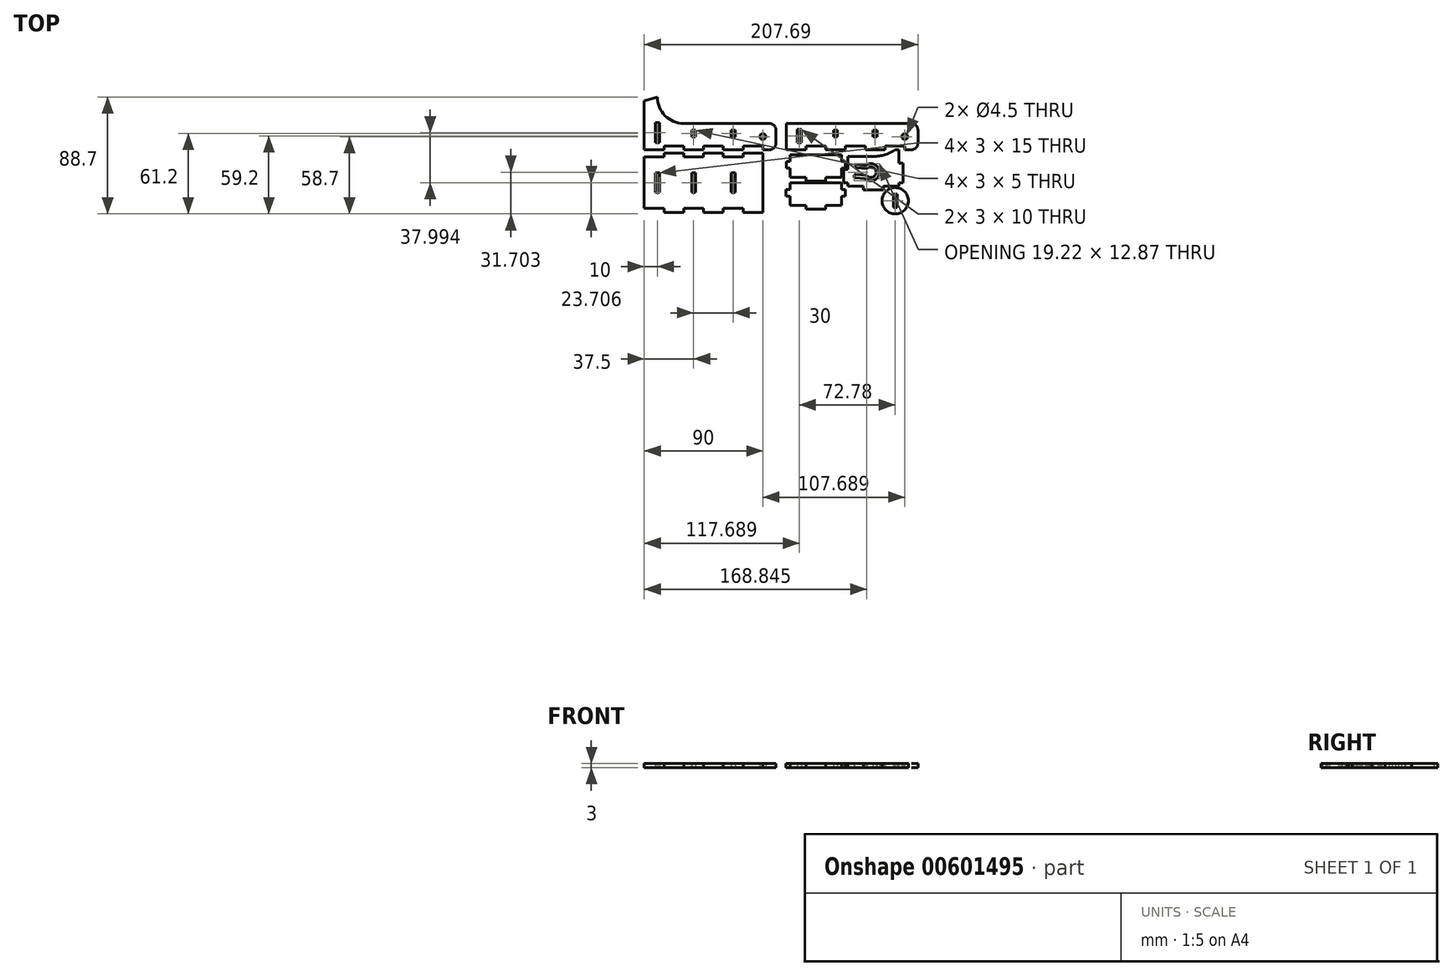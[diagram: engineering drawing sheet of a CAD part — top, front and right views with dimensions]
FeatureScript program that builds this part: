
annotation { "Feature Type Name" : "Feature", "Feature Type Description" : "" }
export const myFeature = defineFeature(function(context is Context, id is Id, definition is map)
    precondition{}
    {
        {
            assignVariable(context, id + "F0", {"name" : "woodTh", "anyValue" : 3});
        }
        {
            var Q0;
            Q0=qCreatedBy(makeId("Top.planeOp"),FACE);
            var sketch = newSketch(context, id + "F1", { "sketchPlane" : qUnion([Q0])});
            skLineSegment(sketch, "E0", {"start": v(10, 40) * mm, "end": v(10, 40) * mm});
            skLineSegment(sketch, "E1", {"start": v(100, 10) * mm, "end": v(90, 10) * mm, "construction": true});
            skCircle(sketch, "E2", {"center": v(90, 10) * mm, "radius": 2.25 * mm});
            skPoint(sketch, "E3.visualSharp", {"position": v(10, 17.5) * mm});
            skArc(sketch, "E3.filletArc", {"start": v(10, 40) * mm, "mid": v(15.86, 25.86) * mm, "end": v(30, 20) * mm});
            skLineSegment(sketch, "E4", {"start": v(0, 0) * mm, "end": v(15, 0) * mm});
            skLineSegment(sketch, "E5", {"start": v(15, 0) * mm, "end": v(15, 3) * mm});
            skLineSegment(sketch, "E6", {"start": v(15, 3) * mm, "end": v(30, 3) * mm});
            skLineSegment(sketch, "E7", {"start": v(30, 3) * mm, "end": v(30, 0) * mm});
            skLineSegment(sketch, "E8.1.0.0", {"start": v(30, 0) * mm, "end": v(45, 0) * mm});
            skLineSegment(sketch, "E8.1.0.1", {"start": v(60, 3) * mm, "end": v(60, 0) * mm});
            skLineSegment(sketch, "E8.1.0.2", {"start": v(45, 3) * mm, "end": v(60, 3) * mm});
            skLineSegment(sketch, "E8.1.0.3", {"start": v(45, 0) * mm, "end": v(45, 3) * mm});
            skLineSegment(sketch, "E8.2.0.0", {"start": v(60, 0) * mm, "end": v(75, 0) * mm});
            skLineSegment(sketch, "E8.2.0.1", {"start": v(90, 3) * mm, "end": v(90, 0) * mm});
            skLineSegment(sketch, "E8.2.0.2", {"start": v(75, 3) * mm, "end": v(90, 3) * mm});
            skLineSegment(sketch, "E8.2.0.3", {"start": v(75, 0) * mm, "end": v(75, 3) * mm});
            skLineSegment(sketch, "E8.direction1", {"start": v(0, 0) * mm, "end": v(30, 0) * mm, "construction": true});
            skLineSegment(sketch, "E9", {"start": v(30, 20) * mm, "end": v(95, 20) * mm});
            skLineSegment(sketch, "E10", {"start": v(100, 15) * mm, "end": v(100, 5) * mm});
            skLineSegment(sketch, "E11", {"start": v(95, 0) * mm, "end": v(90, 0) * mm});
            skPoint(sketch, "E12.visualSharp", {"position": v(100, 20) * mm});
            skArc(sketch, "E12.filletArc", {"start": v(100, 15) * mm, "mid": v(98.54, 18.54) * mm, "end": v(95, 20) * mm});
            skPoint(sketch, "E13.visualSharp", {"position": v(100, 0) * mm});
            skArc(sketch, "E13.filletArc", {"start": v(95, 0) * mm, "mid": v(98.54, 1.46) * mm, "end": v(100, 5) * mm});
            skLineSegment(sketch, "E14", {"start": v(37.5, 20) * mm, "end": v(37.5, 12.5) * mm, "construction": true});
            skPoint(sketch, "E14.startSnap0", {"position": v(37.5, 0) * mm});
            skLineSegment(sketch, "E15.bottom", {"start": v(39, 10) * mm, "end": v(36, 10) * mm});
            skLineSegment(sketch, "E15.top", {"start": v(39, 15) * mm, "end": v(36, 15) * mm});
            skLineSegment(sketch, "E15.left", {"start": v(39, 10) * mm, "end": v(39, 15) * mm});
            skLineSegment(sketch, "E15.right", {"start": v(36, 10) * mm, "end": v(36, 15) * mm});
            skPoint(sketch, "E15.middle", {"position": v(37.5, 12.5) * mm});
            skLineSegment(sketch, "E16", {"start": v(52.5, 3) * mm, "end": v(52.5, 20) * mm, "construction": true});
            skLineSegment(sketch, "E17.MirrorCS", {"start": v(66, 10) * mm, "end": v(66, 15) * mm});
            skPoint(sketch, "E18.MirrorP", {"position": v(67.5, 12.5) * mm});
            skLineSegment(sketch, "E19.MirrorCS", {"start": v(69, 10) * mm, "end": v(69, 15) * mm});
            skLineSegment(sketch, "E20.MirrorCS", {"start": v(66, 10) * mm, "end": v(69, 10) * mm});
            skLineSegment(sketch, "E21.MirrorCS", {"start": v(66, 15) * mm, "end": v(69, 15) * mm});
            skLineSegment(sketch, "E22.MirrorCS", {"start": v(67.5, 20) * mm, "end": v(67.5, 12.5) * mm, "construction": true});
            skLineSegment(sketch, "E23", {"start": v(207.69, 10) * mm, "end": v(197.69, 10) * mm, "construction": true});
            skCircle(sketch, "E24", {"center": v(197.69, 10) * mm, "radius": 2.25 * mm});
            skLineSegment(sketch, "E25", {"start": v(107.69, 0) * mm, "end": v(122.69, 0) * mm});
            skLineSegment(sketch, "E26", {"start": v(122.69, 0) * mm, "end": v(122.69, 3) * mm});
            skLineSegment(sketch, "E27", {"start": v(122.69, 3) * mm, "end": v(137.69, 3) * mm});
            skLineSegment(sketch, "E28", {"start": v(137.69, 3) * mm, "end": v(137.69, 0) * mm});
            skLineSegment(sketch, "E29.1.0.0", {"start": v(137.69, 0) * mm, "end": v(152.69, 0) * mm});
            skLineSegment(sketch, "E29.1.0.1", {"start": v(167.69, 3) * mm, "end": v(167.69, 0) * mm});
            skLineSegment(sketch, "E29.1.0.2", {"start": v(152.69, 3) * mm, "end": v(167.69, 3) * mm});
            skLineSegment(sketch, "E29.1.0.3", {"start": v(152.69, 0) * mm, "end": v(152.69, 3) * mm});
            skLineSegment(sketch, "E29.2.0.0", {"start": v(167.69, 0) * mm, "end": v(182.69, 0) * mm});
            skLineSegment(sketch, "E29.2.0.1", {"start": v(197.69, 3) * mm, "end": v(197.69, 0) * mm});
            skLineSegment(sketch, "E29.2.0.2", {"start": v(182.69, 3) * mm, "end": v(197.69, 3) * mm});
            skLineSegment(sketch, "E29.2.0.3", {"start": v(182.69, 0) * mm, "end": v(182.69, 3) * mm});
            skLineSegment(sketch, "E29.direction1", {"start": v(107.69, 0) * mm, "end": v(137.69, 0) * mm, "construction": true});
            skLineSegment(sketch, "E30", {"start": v(137.69, 20) * mm, "end": v(202.69, 20) * mm});
            skLineSegment(sketch, "E31", {"start": v(207.69, 15) * mm, "end": v(207.69, 5) * mm});
            skLineSegment(sketch, "E32", {"start": v(202.69, 0) * mm, "end": v(197.69, 0) * mm});
            skPoint(sketch, "E33.visualSharp", {"position": v(207.69, 20) * mm});
            skArc(sketch, "E33.filletArc", {"start": v(207.69, 15) * mm, "mid": v(206.22, 18.54) * mm, "end": v(202.69, 20) * mm});
            skPoint(sketch, "E34.visualSharp", {"position": v(207.69, 0) * mm});
            skArc(sketch, "E34.filletArc", {"start": v(202.69, 0) * mm, "mid": v(206.22, 1.46) * mm, "end": v(207.69, 5) * mm});
            skLineSegment(sketch, "E35", {"start": v(145.19, 20) * mm, "end": v(145.19, 12.5) * mm, "construction": true});
            skPoint(sketch, "E35.startSnap0", {"position": v(145.19, 0) * mm});
            skLineSegment(sketch, "E36.bottom", {"start": v(146.69, 10) * mm, "end": v(143.69, 10) * mm});
            skLineSegment(sketch, "E36.top", {"start": v(146.69, 15) * mm, "end": v(143.69, 15) * mm});
            skLineSegment(sketch, "E36.left", {"start": v(146.69, 10) * mm, "end": v(146.69, 15) * mm});
            skLineSegment(sketch, "E36.right", {"start": v(143.69, 10) * mm, "end": v(143.69, 15) * mm});
            skPoint(sketch, "E36.middle", {"position": v(145.19, 12.5) * mm});
            skLineSegment(sketch, "E37", {"start": v(160.19, 3) * mm, "end": v(160.19, 20) * mm, "construction": true});
            skLineSegment(sketch, "E38.MirrorCS", {"start": v(173.69, 10) * mm, "end": v(173.69, 15) * mm});
            skPoint(sketch, "E39.MirrorP", {"position": v(175.19, 12.5) * mm});
            skLineSegment(sketch, "E40.MirrorCS", {"start": v(176.69, 10) * mm, "end": v(176.69, 15) * mm});
            skLineSegment(sketch, "E41.MirrorCS", {"start": v(173.69, 10) * mm, "end": v(176.69, 10) * mm});
            skLineSegment(sketch, "E42.MirrorCS", {"start": v(173.69, 15) * mm, "end": v(176.69, 15) * mm});
            skLineSegment(sketch, "E43.MirrorCS", {"start": v(175.19, 20) * mm, "end": v(175.19, 12.5) * mm, "construction": true});
            skCircle(sketch, "E44", {"center": v(190.47, -38.7) * mm, "radius": 10 * mm});
            skLineSegment(sketch, "E45.bottom", {"start": v(191.97, -43.7) * mm, "end": v(188.97, -43.7) * mm});
            skLineSegment(sketch, "E45.top", {"start": v(191.97, -33.7) * mm, "end": v(188.97, -33.7) * mm});
            skLineSegment(sketch, "E45.left", {"start": v(191.97, -43.7) * mm, "end": v(191.97, -33.7) * mm});
            skLineSegment(sketch, "E45.right", {"start": v(188.97, -43.7) * mm, "end": v(188.97, -33.7) * mm});
            skLineSegment(sketch, "E46", {"start": v(0, -5.5) * mm, "end": v(15, -5.5) * mm});
            skLineSegment(sketch, "E47", {"start": v(15, -5.5) * mm, "end": v(15, -2.5) * mm});
            skLineSegment(sketch, "E48", {"start": v(15, -2.5) * mm, "end": v(30, -2.5) * mm});
            skLineSegment(sketch, "E49", {"start": v(30, -2.5) * mm, "end": v(30, -5.5) * mm});
            skLineSegment(sketch, "E50.1.0.0", {"start": v(30, -5.5) * mm, "end": v(45, -5.5) * mm});
            skLineSegment(sketch, "E50.1.0.1", {"start": v(60, -2.5) * mm, "end": v(60, -5.5) * mm});
            skLineSegment(sketch, "E50.1.0.2", {"start": v(45, -2.5) * mm, "end": v(60, -2.5) * mm});
            skLineSegment(sketch, "E50.1.0.3", {"start": v(45, -5.5) * mm, "end": v(45, -2.5) * mm});
            skLineSegment(sketch, "E50.2.0.0", {"start": v(60, -5.5) * mm, "end": v(75, -5.5) * mm});
            skLineSegment(sketch, "E50.2.0.1", {"start": v(90, -2.5) * mm, "end": v(90, -5.5) * mm});
            skLineSegment(sketch, "E50.2.0.2", {"start": v(75, -2.5) * mm, "end": v(90, -2.5) * mm});
            skLineSegment(sketch, "E50.2.0.3", {"start": v(75, -5.5) * mm, "end": v(75, -2.5) * mm});
            skLineSegment(sketch, "E50.direction1", {"start": v(0, -5.5) * mm, "end": v(30, -5.5) * mm, "construction": true});
            skPoint(sketch, "E51.startSnap0", {"position": v(37.5, -5.5) * mm});
            skLineSegment(sketch, "E52", {"start": v(0, -5.5) * mm, "end": v(0, -25) * mm});
            skLineSegment(sketch, "E53", {"start": v(90, -5.5) * mm, "end": v(90, -25) * mm});
            skLineSegment(sketch, "E54", {"start": v(0, -25) * mm, "end": v(90, -25) * mm, "construction": true});
            skLineSegment(sketch, "E55.MirrorCS", {"start": v(45, -44.5) * mm, "end": v(45, -47.5) * mm});
            skLineSegment(sketch, "E56.MirrorCS", {"start": v(75, -44.5) * mm, "end": v(75, -47.5) * mm});
            skLineSegment(sketch, "E57.MirrorCS", {"start": v(30, -47.5) * mm, "end": v(30, -44.5) * mm});
            skLineSegment(sketch, "E58.MirrorCS", {"start": v(90, -47.5) * mm, "end": v(90, -44.5) * mm});
            skLineSegment(sketch, "E59.MirrorCS", {"start": v(60, -47.5) * mm, "end": v(60, -44.5) * mm});
            skLineSegment(sketch, "E60.MirrorCS", {"start": v(15, -44.5) * mm, "end": v(15, -47.5) * mm});
            skLineSegment(sketch, "E61.MirrorCS", {"start": v(0, -44.5) * mm, "end": v(15, -44.5) * mm});
            skLineSegment(sketch, "E62.MirrorCS", {"start": v(0, -44.5) * mm, "end": v(0, -25) * mm});
            skLineSegment(sketch, "E63.MirrorCS", {"start": v(45, -47.5) * mm, "end": v(60, -47.5) * mm});
            skLineSegment(sketch, "E64.MirrorCS", {"start": v(90, -44.5) * mm, "end": v(90, -25) * mm});
            skPoint(sketch, "E65.MirrorP", {"position": v(37.5, -44.5) * mm});
            skLineSegment(sketch, "E66.MirrorCS", {"start": v(30, -44.5) * mm, "end": v(45, -44.5) * mm});
            skLineSegment(sketch, "E67.MirrorCS", {"start": v(75, -47.5) * mm, "end": v(90, -47.5) * mm});
            skLineSegment(sketch, "E68.MirrorCS", {"start": v(60, -44.5) * mm, "end": v(75, -44.5) * mm});
            skLineSegment(sketch, "E69.MirrorCS", {"start": v(15, -47.5) * mm, "end": v(30, -47.5) * mm});
            skLineSegment(sketch, "E70", {"start": v(10, 3) * mm, "end": v(10, 13) * mm, "construction": true});
            skLineSegment(sketch, "E71.bottom", {"start": v(11.5, 5.5) * mm, "end": v(8.5, 5.5) * mm});
            skLineSegment(sketch, "E71.top", {"start": v(11.5, 20.5) * mm, "end": v(8.5, 20.5) * mm});
            skLineSegment(sketch, "E71.left", {"start": v(11.5, 5.5) * mm, "end": v(11.5, 20.5) * mm});
            skLineSegment(sketch, "E71.right", {"start": v(8.5, 5.5) * mm, "end": v(8.5, 20.5) * mm});
            skPoint(sketch, "E71.middle", {"position": v(10, 13) * mm});
            skLineSegment(sketch, "E72", {"start": v(107.69, 0) * mm, "end": v(107.69, 20) * mm});
            skLineSegment(sketch, "E73", {"start": v(107.69, 20) * mm, "end": v(137.69, 20) * mm});
            skLineSegment(sketch, "E74", {"start": v(107.69, 20) * mm, "end": v(117.69, 20) * mm, "construction": true});
            skLineSegment(sketch, "E75", {"start": v(117.69, 3) * mm, "end": v(117.69, 10.5) * mm, "construction": true});
            skLineSegment(sketch, "E76.bottom", {"start": v(119.19, 5.5) * mm, "end": v(116.19, 5.5) * mm});
            skLineSegment(sketch, "E76.top", {"start": v(119.19, 15.5) * mm, "end": v(116.19, 15.5) * mm});
            skLineSegment(sketch, "E76.left", {"start": v(119.19, 5.5) * mm, "end": v(119.19, 15.5) * mm});
            skLineSegment(sketch, "E76.right", {"start": v(116.19, 5.5) * mm, "end": v(116.19, 15.5) * mm});
            skPoint(sketch, "E76.middle", {"position": v(117.69, 10.5) * mm});
            skLineSegment(sketch, "E77", {"start": v(0, -25) * mm, "end": v(10, -25) * mm, "construction": true});
            skLineSegment(sketch, "E78.bottom", {"start": v(11.5, -32.5) * mm, "end": v(8.5, -32.5) * mm});
            skLineSegment(sketch, "E78.top", {"start": v(11.5, -17.5) * mm, "end": v(8.5, -17.5) * mm});
            skLineSegment(sketch, "E78.left", {"start": v(11.5, -32.5) * mm, "end": v(11.5, -17.5) * mm});
            skLineSegment(sketch, "E78.right", {"start": v(8.5, -32.5) * mm, "end": v(8.5, -17.5) * mm});
            skPoint(sketch, "E78.middle", {"position": v(10, -25) * mm});
            skLineSegment(sketch, "E79.bottom", {"start": v(39, -32.5) * mm, "end": v(36, -32.5) * mm});
            skLineSegment(sketch, "E79.top", {"start": v(39, -17.5) * mm, "end": v(36, -17.5) * mm});
            skLineSegment(sketch, "E79.left", {"start": v(39, -32.5) * mm, "end": v(39, -17.5) * mm});
            skLineSegment(sketch, "E79.right", {"start": v(36, -32.5) * mm, "end": v(36, -17.5) * mm});
            skPoint(sketch, "E79.middle", {"position": v(37.5, -25) * mm});
            skLineSegment(sketch, "E80.bottom", {"start": v(69, -32.5) * mm, "end": v(66, -32.5) * mm});
            skLineSegment(sketch, "E80.top", {"start": v(69, -17.5) * mm, "end": v(66, -17.5) * mm});
            skLineSegment(sketch, "E80.left", {"start": v(69, -32.5) * mm, "end": v(69, -17.5) * mm});
            skLineSegment(sketch, "E80.right", {"start": v(66, -32.5) * mm, "end": v(66, -17.5) * mm});
            skPoint(sketch, "E80.middle", {"position": v(67.5, -25) * mm});
            skPoint(sketch, "E81", {"position": v(67.5, -5.5) * mm});
            skLineSegment(sketch, "E82", {"start": v(110.69, -3.83) * mm, "end": v(130.19, -3.83) * mm});
            skLineSegment(sketch, "E83", {"start": v(110.69, -3.83) * mm, "end": v(110.69, -8.83) * mm});
            skLineSegment(sketch, "E84", {"start": v(110.69, -8.83) * mm, "end": v(107.69, -8.83) * mm});
            skLineSegment(sketch, "E85", {"start": v(107.69, -8.83) * mm, "end": v(107.69, -13.83) * mm});
            skLineSegment(sketch, "E86", {"start": v(107.69, -13.83) * mm, "end": v(110.69, -13.83) * mm});
            skLineSegment(sketch, "E87", {"start": v(110.69, -13.83) * mm, "end": v(110.69, -20.83) * mm});
            skLineSegment(sketch, "E88", {"start": v(110.69, -20.83) * mm, "end": v(122.69, -20.83) * mm});
            skLineSegment(sketch, "E89", {"start": v(122.69, -20.83) * mm, "end": v(122.69, -23.83) * mm});
            skLineSegment(sketch, "E90", {"start": v(122.69, -23.83) * mm, "end": v(130.19, -23.83) * mm});
            skLineSegment(sketch, "E91", {"start": v(130.19, -3.83) * mm, "end": v(130.19, -23.83) * mm, "construction": true});
            skLineSegment(sketch, "E92.MirrorCS", {"start": v(152.69, -13.83) * mm, "end": v(149.69, -13.83) * mm});
            skLineSegment(sketch, "E93.MirrorCS", {"start": v(137.69, -20.83) * mm, "end": v(137.69, -23.83) * mm});
            skLineSegment(sketch, "E94.MirrorCS", {"start": v(137.69, -23.83) * mm, "end": v(130.19, -23.83) * mm});
            skLineSegment(sketch, "E95.MirrorCS", {"start": v(149.69, -13.83) * mm, "end": v(149.69, -20.83) * mm});
            skLineSegment(sketch, "E96.MirrorCS", {"start": v(149.69, -3.83) * mm, "end": v(130.19, -3.83) * mm});
            skLineSegment(sketch, "E97.MirrorCS", {"start": v(149.69, -20.83) * mm, "end": v(137.69, -20.83) * mm});
            skLineSegment(sketch, "E98.MirrorCS", {"start": v(149.69, -8.83) * mm, "end": v(152.69, -8.83) * mm});
            skLineSegment(sketch, "E99.MirrorCS", {"start": v(149.69, -3.83) * mm, "end": v(149.69, -8.83) * mm});
            skLineSegment(sketch, "E100.MirrorCS", {"start": v(152.69, -8.83) * mm, "end": v(152.69, -13.83) * mm});
            skLineSegment(sketch, "E101", {"start": v(110.6, -25.22) * mm, "end": v(130.1, -25.22) * mm});
            skLineSegment(sketch, "E102", {"start": v(110.6, -25.22) * mm, "end": v(110.6, -30.22) * mm});
            skLineSegment(sketch, "E103", {"start": v(110.6, -30.22) * mm, "end": v(107.6, -30.22) * mm});
            skLineSegment(sketch, "E104", {"start": v(107.6, -30.22) * mm, "end": v(107.6, -35.22) * mm});
            skLineSegment(sketch, "E105", {"start": v(107.6, -35.22) * mm, "end": v(110.6, -35.22) * mm});
            skLineSegment(sketch, "E106", {"start": v(110.6, -35.22) * mm, "end": v(110.6, -42.22) * mm});
            skLineSegment(sketch, "E107", {"start": v(110.6, -42.22) * mm, "end": v(122.6, -42.22) * mm});
            skLineSegment(sketch, "E108", {"start": v(122.6, -42.22) * mm, "end": v(122.6, -45.22) * mm});
            skLineSegment(sketch, "E109", {"start": v(122.6, -45.22) * mm, "end": v(130.1, -45.22) * mm});
            skLineSegment(sketch, "E110", {"start": v(130.1, -25.22) * mm, "end": v(130.1, -45.22) * mm, "construction": true});
            skLineSegment(sketch, "E111.MirrorCS", {"start": v(152.6, -35.22) * mm, "end": v(149.6, -35.22) * mm});
            skLineSegment(sketch, "E112.MirrorCS", {"start": v(137.6, -42.22) * mm, "end": v(137.6, -45.22) * mm});
            skLineSegment(sketch, "E113.MirrorCS", {"start": v(137.6, -45.22) * mm, "end": v(130.1, -45.22) * mm});
            skLineSegment(sketch, "E114.MirrorCS", {"start": v(149.6, -35.22) * mm, "end": v(149.6, -42.22) * mm});
            skLineSegment(sketch, "E115.MirrorCS", {"start": v(149.6, -25.22) * mm, "end": v(130.1, -25.22) * mm});
            skLineSegment(sketch, "E116.MirrorCS", {"start": v(149.6, -42.22) * mm, "end": v(137.6, -42.22) * mm});
            skLineSegment(sketch, "E117.MirrorCS", {"start": v(149.6, -30.22) * mm, "end": v(152.6, -30.22) * mm});
            skLineSegment(sketch, "E118.MirrorCS", {"start": v(149.6, -25.22) * mm, "end": v(149.6, -30.22) * mm});
            skLineSegment(sketch, "E119.MirrorCS", {"start": v(152.6, -30.22) * mm, "end": v(152.6, -35.22) * mm});
            skLineSegment(sketch, "E120", {"start": v(154.37, -27.52) * mm, "end": v(154.37, -25.02) * mm});
            skLineSegment(sketch, "E121", {"start": v(154.37, -25.02) * mm, "end": v(151.37, -25.02) * mm});
            skLineSegment(sketch, "E122", {"start": v(151.37, -25.02) * mm, "end": v(151.37, -15.02) * mm});
            skLineSegment(sketch, "E123", {"start": v(151.37, -15.02) * mm, "end": v(154.37, -15.02) * mm});
            skLineSegment(sketch, "E124", {"start": v(154.37, -27.52) * mm, "end": v(166.37, -27.52) * mm});
            skLineSegment(sketch, "E125", {"start": v(166.37, -27.52) * mm, "end": v(166.37, -30.52) * mm});
            skLineSegment(sketch, "E126", {"start": v(166.37, -30.52) * mm, "end": v(173.87, -30.52) * mm});
            skLineSegment(sketch, "E127", {"start": v(173.87, -5.02) * mm, "end": v(173.87, -30.52) * mm, "construction": true});
            skLineSegment(sketch, "E128.MirrorCS", {"start": v(181.37, -27.52) * mm, "end": v(181.37, -30.52) * mm});
            skLineSegment(sketch, "E129.MirrorCS", {"start": v(181.37, -30.52) * mm, "end": v(173.87, -30.52) * mm});
            skLineSegment(sketch, "E130.MirrorCS", {"start": v(193.37, -27.52) * mm, "end": v(181.37, -27.52) * mm});
            skLineSegment(sketch, "E131", {"start": v(154.37, -15.02) * mm, "end": v(154.37, -5.02) * mm});
            skLineSegment(sketch, "E132", {"start": v(154.37, -5.02) * mm, "end": v(173.87, -5.02) * mm});
            skLineSegment(sketch, "E133.MirrorCS", {"start": v(193.37, -25.02) * mm, "end": v(196.37, -25.02) * mm});
            skLineSegment(sketch, "E134.MirrorCS", {"start": v(193.37, -27.52) * mm, "end": v(193.37, -25.02) * mm});
            skLineSegment(sketch, "E135", {"start": v(196.37, -25.02) * mm, "end": v(196.37, -10.02) * mm});
            skLineSegment(sketch, "E136", {"start": v(196.37, -10.02) * mm, "end": v(193.37, -10.02) * mm});
            skLineSegment(sketch, "E137", {"start": v(193.37, -10.02) * mm, "end": v(193.37, -0.02) * mm});
            skLineSegment(sketch, "E138", {"start": v(193.37, -0.02) * mm, "end": v(190.37, -0.02) * mm});
            skLineSegment(sketch, "E139", {"start": v(167.15, -14.23) * mm, "end": v(169.02, -14.35) * mm});
            skLineSegment(sketch, "E140", {"start": v(167.15, -14.23) * mm, "end": v(160.66, -13.8) * mm});
            skLineSegment(sketch, "E141.0", {"start": v(166.82, -19.22) * mm, "end": v(168.69, -19.34) * mm});
            skLineSegment(sketch, "E141.1", {"start": v(166.82, -19.22) * mm, "end": v(160.33, -18.79) * mm});
            skLineSegment(sketch, "E142", {"start": v(172.14, -14.56) * mm, "end": v(171.8, -19.55) * mm, "construction": true});
            skArc(sketch, "E143", {"start": v(168.69, -19.34) * mm, "mid": v(175.96, -17.32) * mm, "end": v(169.02, -14.35) * mm});
            skLineSegment(sketch, "E144.0", {"start": v(166.65, -21.71) * mm, "end": v(160.17, -21.28) * mm});
            skLineSegment(sketch, "E144.1", {"start": v(167.31, -11.73) * mm, "end": v(160.83, -11.3) * mm});
            skLineSegment(sketch, "E144.2", {"start": v(167.31, -11.73) * mm, "end": v(168.16, -11.79) * mm});
            skArc(sketch, "E144.3", {"start": v(167.5, -21.77) * mm, "mid": v(178.46, -17.48) * mm, "end": v(168.16, -11.79) * mm});
            skLineSegment(sketch, "E144.4", {"start": v(166.65, -21.71) * mm, "end": v(167.5, -21.77) * mm});
            skLineSegment(sketch, "E145", {"start": v(159.27, -19.72) * mm, "end": v(159.23, -20.22) * mm});
            skLineSegment(sketch, "E146", {"start": v(159.73, -12.73) * mm, "end": v(159.76, -12.23) * mm});
            skPoint(sketch, "E147.visualSharp", {"position": v(159.83, -11.24) * mm});
            skArc(sketch, "E147.filletArc", {"start": v(160.83, -11.3) * mm, "mid": v(160.1, -11.55) * mm, "end": v(159.76, -12.23) * mm});
            skPoint(sketch, "E148.visualSharp", {"position": v(159.66, -13.73) * mm});
            skArc(sketch, "E148.filletArc", {"start": v(159.73, -12.73) * mm, "mid": v(159.97, -13.46) * mm, "end": v(160.66, -13.8) * mm});
            skPoint(sketch, "E149.visualSharp", {"position": v(159.33, -18.72) * mm});
            skArc(sketch, "E149.filletArc", {"start": v(160.33, -18.79) * mm, "mid": v(159.6, -19.03) * mm, "end": v(159.27, -19.72) * mm});
            skPoint(sketch, "E150.visualSharp", {"position": v(159.17, -21.21) * mm});
            skArc(sketch, "E150.filletArc", {"start": v(159.23, -20.22) * mm, "mid": v(159.48, -20.94) * mm, "end": v(160.17, -21.28) * mm});
            skArc(sketch, "E151", {"start": v(173.87, -5.02) * mm, "mid": v(182.49, -3.74) * mm, "end": v(190.37, -0.02) * mm});
            skLineSegment(sketch, "E152", {"start": v(0, 0) * mm, "end": v(0, 37) * mm});
            skLineSegment(sketch, "E153", {"start": v(0, 37) * mm, "end": v(10, 40) * mm});
            skLineSegment(sketch, "E154.bottom", {"start": v(-69.28, 203.48) * mm, "end": v(230.72, 203.48) * mm, "construction": true});
            skLineSegment(sketch, "E154.top", {"start": v(-69.28, -96.52) * mm, "end": v(230.72, -96.52) * mm, "construction": true});
            skLineSegment(sketch, "E154.left", {"start": v(-69.28, 203.48) * mm, "end": v(-69.28, -96.52) * mm, "construction": true});
            skLineSegment(sketch, "E154.right", {"start": v(230.72, 203.48) * mm, "end": v(230.72, -96.52) * mm, "construction": true});
            skSolve(sketch);
        }
        {
            var Q0;
            Q0=makeQuery(id+"F1.imprint","IMPRINT",FACE,{"disambiguationData":[TD([[makeQuery(id+"F1.imprint","IMPRINT",EDGE,{"derivedFrom":sQuery(id+"F1.wireOp",EDGE,"E44")}),1.0]])]});
            var Q1;
            Q1=makeQuery(id+"F1.imprint","IMPRINT",FACE,{"disambiguationData":[TD([[makeQuery(id+"F1.imprint","IMPRINT",EDGE,{"derivedFrom":sQuery(id+"F1.wireOp",EDGE,"E120")}),-1.0]])]});
            var Q2;
            Q2=makeQuery(id+"F1.imprint","IMPRINT",FACE,{"disambiguationData":[TD([[makeQuery(id+"F1.imprint","IMPRINT",EDGE,{"derivedFrom":sQuery(id+"F1.wireOp",EDGE,"UyCQDnug-uUNh-rQK7-pMAH-MDYSq2HAjCCW")}),-1.0]])]});
            var Q3;
            Q3=makeQuery(id+"F1.imprint","IMPRINT",FACE,{"disambiguationData":[TD([[makeQuery(id+"F1.imprint","IMPRINT",EDGE,{"derivedFrom":sQuery(id+"F1.wireOp",EDGE,"E24")}),-1.0]])]});
            var Q4;
            Q4=makeQuery(id+"F1.imprint","IMPRINT",FACE,{"disambiguationData":[TD([[makeQuery(id+"F1.imprint","IMPRINT",EDGE,{"derivedFrom":sQuery(id+"F1.wireOp",EDGE,"E46")}),-1.0]])]});
            var Q5;
            Q5=makeQuery(id+"F1.imprint","IMPRINT",FACE,{"disambiguationData":[TD([[makeQuery(id+"F1.imprint","IMPRINT",EDGE,{"derivedFrom":sQuery(id+"F1.wireOp",EDGE,"E82")}),-1.0]])]});
            var Q6;
            Q6=makeQuery(id+"F1.imprint","IMPRINT",FACE,{"disambiguationData":[TD([[makeQuery(id+"F1.imprint","IMPRINT",EDGE,{"derivedFrom":sQuery(id+"F1.wireOp",EDGE,"E101")}),-1.0]])]});
            var Q7;
            Q7=makeQuery(id+"F1.imprint","IMPRINT",FACE,{"disambiguationData":[TD([[makeQuery(id+"F1.imprint","IMPRINT",EDGE,{"derivedFrom":sQuery(id+"F1.wireOp",EDGE,"E2")}),-1.0]])]});
            extrude(context, id + "F2", {"entities" : qUnion([Q0, Q1, Q2, Q3, Q4, Q5, Q6, Q7]), "depth" : (getVariable(context, 'woodTh')) * mm, "offsetDistance" : 25 * mm});
        }
    });
